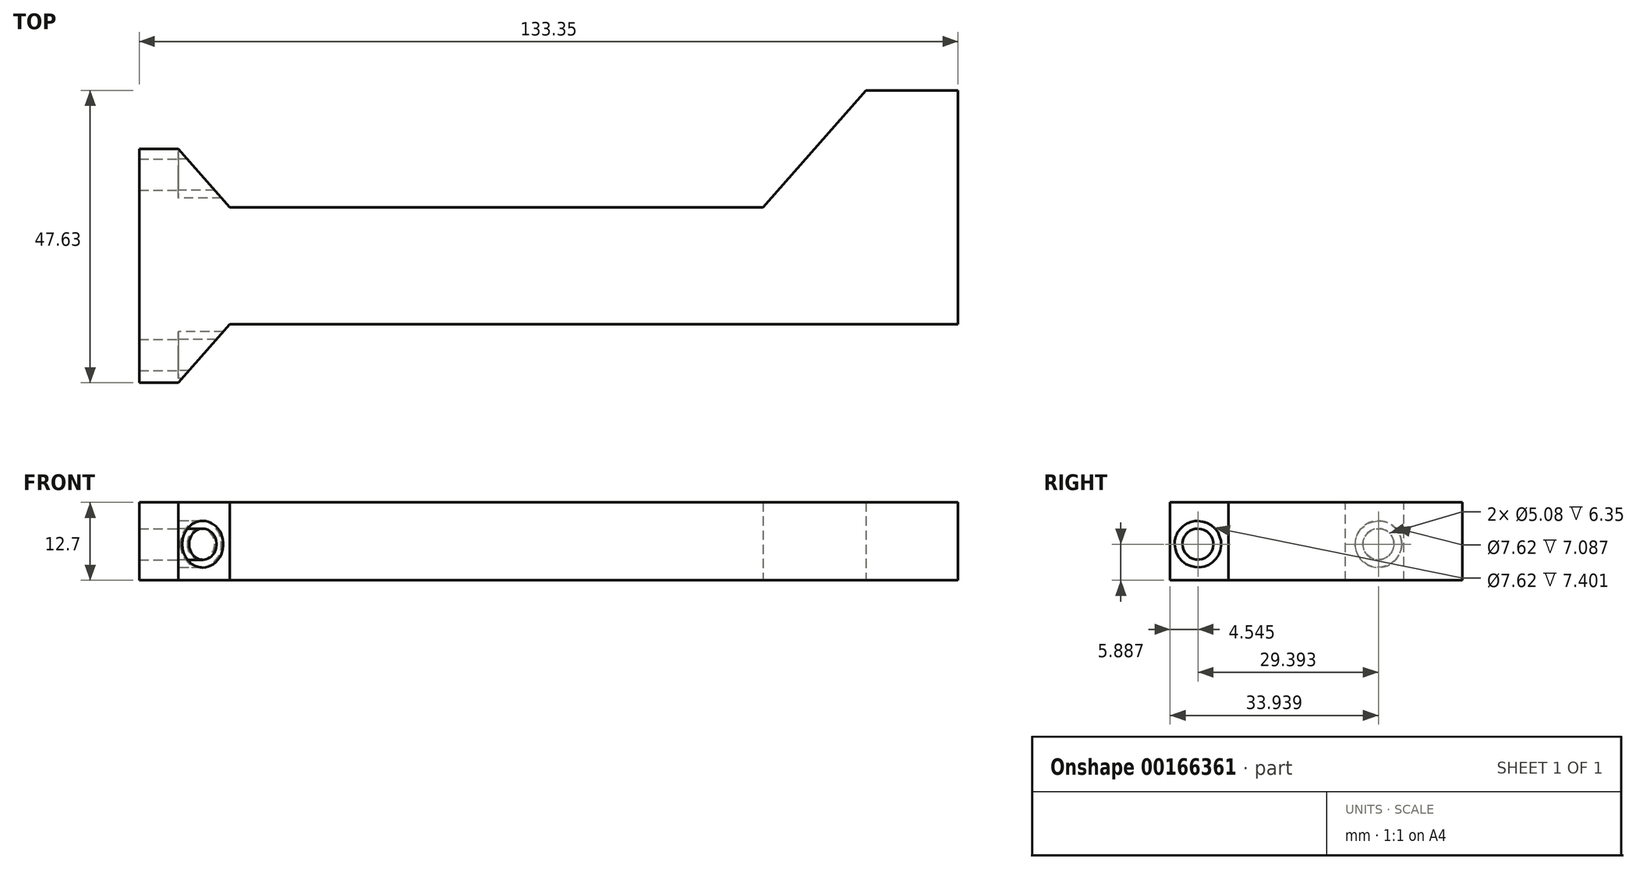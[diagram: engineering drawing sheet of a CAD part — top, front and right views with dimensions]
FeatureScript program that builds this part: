
annotation { "Feature Type Name" : "Feature", "Feature Type Description" : "" }
export const myFeature = defineFeature(function(context is Context, id is Id, definition is map)
    precondition{}
    {
        {
            var Q0;
            Q0=qCreatedBy(makeId("Top.planeOp"),FACE);
            var sketch = newSketch(context, id + "F0", { "sketchPlane" : qUnion([Q0])});
            skLineSegment(sketch, "E0.bottom", {"start": v(-63.5, 19.05) * mm, "end": v(63.5, 19.05) * mm});
            skLineSegment(sketch, "E0.top", {"start": v(-63.5, -19.05) * mm, "end": v(63.5, -19.05) * mm});
            skLineSegment(sketch, "E0.left", {"start": v(-63.5, 19.05) * mm, "end": v(-63.5, -19.05) * mm});
            skLineSegment(sketch, "E0.right", {"start": v(63.5, 19.05) * mm, "end": v(63.5, -19.05) * mm});
            skPoint(sketch, "E0.middle", {"position": v(0, 0) * mm});
            skLineSegment(sketch, "E1", {"start": v(-63.5, 19.05) * mm, "end": v(-63.5, 0) * mm});
            skLineSegment(sketch, "E2", {"start": v(-63.5, 0) * mm, "end": v(31.75, 0) * mm});
            skLineSegment(sketch, "E3", {"start": v(31.75, 0) * mm, "end": v(48.55, 19.05) * mm});
            skSolve(sketch);
        }
        {
            var Q0;
            Q0=makeQuery(id+"F0.imprint","IMPRINT",FACE,{"disambiguationData":[TD([[makeQuery(id+"F0.imprint","IMPRINT",EDGE,{"derivedFrom":sQuery(id+"F0.wireOp",EDGE,"E0.top")}),1.0]])]});
            extrude(context, id + "F1", {"entities" : qUnion([Q0]), "depth" : 12.7 * mm});
        }
        {
            var Q0;
            Q0=makeQuery(id+"F1.opExtrude","SWEPT_FACE",FACE,{"disambiguationData":[OSD([sQuery(id+"F0.wireOp",EDGE,"E0.left")])]});
            var sketch = newSketch(context, id + "F2", { "sketchPlane" : qUnion([Q0])});
            skLineSegment(sketch, "E4.bottom", {"start": v(-9.52, 0) * mm, "end": v(28.58, 0) * mm});
            skLineSegment(sketch, "E4.top", {"start": v(-9.52, 12.7) * mm, "end": v(28.58, 12.7) * mm});
            skLineSegment(sketch, "E4.left", {"start": v(-9.52, 0) * mm, "end": v(-9.52, 12.7) * mm});
            skLineSegment(sketch, "E4.right", {"start": v(28.58, 0) * mm, "end": v(28.58, 12.7) * mm});
            skPoint(sketch, "E4.middle", {"position": v(9.53, 6.35) * mm});
            skCircle(sketch, "E5", {"center": v(-5.36, 5.89) * mm, "radius": 2.54 * mm});
            skCircle(sketch, "E6", {"center": v(24.03, 5.89) * mm, "radius": 2.54 * mm});
            skSolve(sketch);
        }
        {
            var Q0;
            {var subQ1=sQuery(id+"F0.wireOp",EDGE,"E0.left");var subQ2=makeQuery(id+"F1.opExtrude","SWEPT_EDGE",EDGE,{"disambiguationData":[OSD([sQuery(id+"F0.wireOp",EDGE,"E0.top"),subQ1])]});Q0=makeQuery(id+"F2.imprint","IMPRINT",FACE,{"disambiguationData":[TD([[makeQuery(id+"F2.imprint","IMPRINT",EDGE,{"derivedFrom":subQ2}),-1.0]])]});}
            var Q1;
            {var subQ2=sQuery(id+"F2.wireOp",EDGE,"E4.left");Q1=makeQuery(id+"F2.imprint","IMPRINT",FACE,{"disambiguationData":[TD([[makeQuery(id+"F2.imprint","IMPRINT",EDGE,{"derivedFrom":subQ2}),-1.0]])]});}
            var Q2;
            {var subQ2=sQuery(id+"F2.wireOp",EDGE,"E4.right");Q2=makeQuery(id+"F2.imprint","IMPRINT",FACE,{"disambiguationData":[TD([[makeQuery(id+"F2.imprint","IMPRINT",EDGE,{"derivedFrom":subQ2}),1.0]])]});}
            extrude(context, id + "F3", {"entities" : qUnion([Q0, Q1, Q2]), "operationType" : NewBodyOperationType.ADD, "depth" : 6.35 * mm});
        }
        {
            var Q0;
            Q0=makeQuery(id+"F2.imprint","IMPRINT",FACE,{"disambiguationData":[TD([[makeQuery(id+"F2.imprint","IMPRINT",EDGE,{"derivedFrom":sQuery(id+"F2.wireOp",EDGE,"E6")}),1.0]])]});
            extrude(context, id + "F4", {"entities" : qUnion([Q0]), "operationType" : NewBodyOperationType.REMOVE, "depth" : 25.4 * mm});
        }
        {
            var Q0;
            Q0=makeQuery(id+"F3.boolean.opBoolean","MERGE",FACE,{"derivedFrom":[makeQuery(id+"F1.opExtrude","CAP_FACE",FACE,{"disambiguationData":[OSD([sQuery(id+"F0.wireOp",EDGE,"E0.bottom"),sQuery(id+"F0.wireOp",EDGE,"E0.top"),sQuery(id+"F0.wireOp",EDGE,"E0.left"),sQuery(id+"F0.wireOp",EDGE,"E0.right"),sQuery(id+"F0.wireOp",EDGE,"E2"),sQuery(id+"F0.wireOp",EDGE,"E3")])],"isStart":false}),makeQuery(id+"F3.opExtrude","SWEPT_FACE",FACE,{"disambiguationData":[OSD([sQuery(id+"F2.wireOp",EDGE,"E4.top")])]})]});
            var sketch = newSketch(context, id + "F5", { "sketchPlane" : qUnion([Q0])});
            skPoint(sketch, "E7.endSnap0", {"position": v(-66.67, 9.53) * mm});
            skLineSegment(sketch, "E8", {"start": v(-63.5, 9.53) * mm, "end": v(-55.1, 0) * mm});
            skLineSegment(sketch, "E9", {"start": v(-63.5, -28.57) * mm, "end": v(-55.11, -19.05) * mm});
            skSolve(sketch);
        }
        {
            var Q0;
            {var subQ0=sQuery(id+"F5.wireOp",EDGE,"E8");Q0=makeQuery(id+"F5.imprint","IMPRINT",FACE,{"disambiguationData":[TD([[makeQuery(id+"F5.imprint","IMPRINT",EDGE,{"derivedFrom":subQ0}),-1.0]])]});}
            extrude(context, id + "F6", {"entities" : qUnion([Q0]), "operationType" : NewBodyOperationType.ADD, "oppositeDirection" : true, "depth" : 12.7 * mm});
        }
        {
            var Q0;
            {var subQ0=sQuery(id+"F5.wireOp",EDGE,"E9");Q0=makeQuery(id+"F5.imprint","IMPRINT",FACE,{"disambiguationData":[TD([[makeQuery(id+"F5.imprint","IMPRINT",EDGE,{"derivedFrom":subQ0}),1.0]])]});}
            extrude(context, id + "F7", {"entities" : qUnion([Q0]), "operationType" : NewBodyOperationType.ADD, "oppositeDirection" : true, "depth" : 12.7 * mm});
        }
        {
            var Q0;
            Q0=makeQuery(id+"F6.opExtrude","SWEPT_FACE",FACE,{"disambiguationData":[OSD([sQuery(id+"F2.wireOp",EDGE,"E4.top")])]});
            var sketch = newSketch(context, id + "F8", { "sketchPlane" : qUnion([Q0])});
            skCircle(sketch, "E10", {"center": v(-5.36, 5.89) * mm, "radius": 3.81 * mm});
            skSolve(sketch);
        }
        {
            var Q0;
            Q0=makeQuery(id+"F8.imprint","IMPRINT",FACE,{"disambiguationData":[TD([[makeQuery(id+"F8.imprint","IMPRINT",EDGE,{"derivedFrom":sQuery(id+"F8.wireOp",EDGE,"E10")}),1.0]])]});
            var Q1;
            Q1=makeQuery(id+"F8.imprint","IMPRINT",FACE,{"disambiguationData":[TD([[makeQuery(id+"F8.imprint","IMPRINT",EDGE,{"derivedFrom":makeQuery(id+"F3.opExtrude","CAP_EDGE",EDGE,{"disambiguationData":[OSD([sQuery(id+"F2.wireOp",EDGE,"E5")])],"isStart":true})}),1.0]])]});
            extrude(context, id + "F9", {"entities" : qUnion([Q0, Q1]), "operationType" : NewBodyOperationType.REMOVE, "oppositeDirection" : true, "depth" : 25.4 * mm});
        }
        {
            var Q0;
            Q0=makeQuery(id+"F7.opExtrude","SWEPT_FACE",FACE,{"disambiguationData":[OSD([sQuery(id+"F2.wireOp",EDGE,"E4.top")])]});
            var sketch = newSketch(context, id + "F10", { "sketchPlane" : qUnion([Q0])});
            skCircle(sketch, "E11", {"center": v(24.03, 5.89) * mm, "radius": 3.81 * mm});
            skSolve(sketch);
        }
        {
            var Q0;
            Q0=makeQuery(id+"F10.imprint","IMPRINT",FACE,{"disambiguationData":[TD([[makeQuery(id+"F10.imprint","IMPRINT",EDGE,{"derivedFrom":makeQuery(id+"F3.opExtrude","CAP_EDGE",EDGE,{"disambiguationData":[OSD([sQuery(id+"F2.wireOp",EDGE,"E6")])],"isStart":true})}),1.0]])]});
            var Q1;
            Q1=makeQuery(id+"F10.imprint","IMPRINT",FACE,{"disambiguationData":[TD([[makeQuery(id+"F10.imprint","IMPRINT",EDGE,{"derivedFrom":sQuery(id+"F10.wireOp",EDGE,"E11")}),1.0]])]});
            extrude(context, id + "F11", {"entities" : qUnion([Q0, Q1]), "operationType" : NewBodyOperationType.REMOVE, "oppositeDirection" : true, "depth" : 25.4 * mm});
        }
    });
